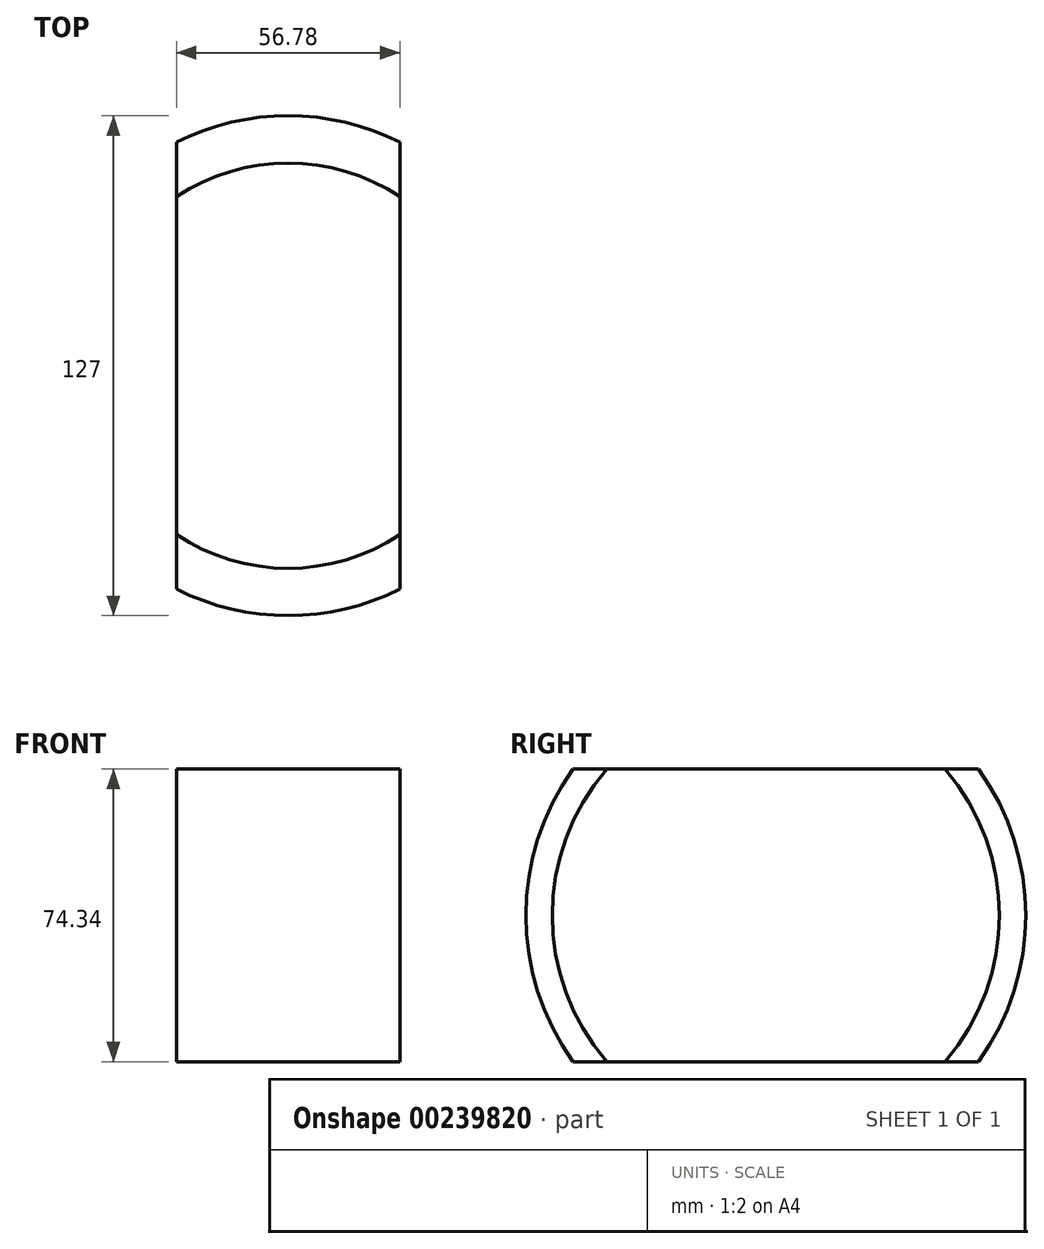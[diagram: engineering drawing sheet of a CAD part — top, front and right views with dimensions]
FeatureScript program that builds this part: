
annotation { "Feature Type Name" : "Feature", "Feature Type Description" : "" }
export const myFeature = defineFeature(function(context is Context, id is Id, definition is map)
    precondition{}
    {
        {
            var Q0;
            Q0=qCreatedBy(makeId("Front.planeOp"),FACE);
            var sketch = newSketch(context, id + "F0", { "sketchPlane" : qUnion([Q0])});
            skLineSegment(sketch, "E0.bottom", {"start": v(28.39, 37.17) * mm, "end": v(-28.39, 37.17) * mm});
            skLineSegment(sketch, "E0.top", {"start": v(28.39, -37.17) * mm, "end": v(-28.39, -37.17) * mm});
            skLineSegment(sketch, "E0.left", {"start": v(28.39, 37.17) * mm, "end": v(28.39, -37.17) * mm});
            skLineSegment(sketch, "E0.right", {"start": v(-28.39, 37.17) * mm, "end": v(-28.39, -37.17) * mm});
            skPoint(sketch, "E0.middle", {"position": v(0, 0) * mm});
            skSolve(sketch);
        }
        {
            var Q0;
            Q0 = qSketchRegion(id + "F0", true);
            extrude(context, id + "F1", {"entities" : qUnion([Q0]), "endBound" : BoundingType.SYMMETRIC, "depth" : 127 * mm});
        }
        {
            var Q0;
            Q0=qCreatedBy(makeId("Right.planeOp"),FACE);
            var sketch = newSketch(context, id + "F2", { "sketchPlane" : qUnion([Q0])});
            skArc(sketch, "E1", {"start": v(51.44, -37.23) * mm, "mid": v(63.5, 0) * mm, "end": v(51.44, 37.23) * mm});
            skLineSegment(sketch, "E2", {"start": v(51.44, 37.23) * mm, "end": v(51.44, -37.23) * mm, "construction": true});
            skLineSegment(sketch, "E3", {"start": v(0, 0) * mm, "end": v(51.44, 0) * mm, "construction": true});
            skLineSegment(sketch, "E4", {"start": v(51.44, 37.23) * mm, "end": v(80.73, 43.93) * mm});
            skLineSegment(sketch, "E5", {"start": v(80.73, 43.93) * mm, "end": v(80.73, -55.34) * mm});
            skLineSegment(sketch, "E6", {"start": v(80.73, -55.34) * mm, "end": v(51.44, -37.23) * mm});
            skLineSegment(sketch, "E7", {"start": v(0, 0) * mm, "end": v(0, -64.57) * mm, "construction": true});
            skSolve(sketch);
        }
        {
            var Q0;
            Q0 = qSketchRegion(id + "F2", true);
            var Q1;
            Q1=sQuery(id+"F2.wireOp",EDGE,"E7");
            revolve(context, id + "F3", {"operationType" : NewBodyOperationType.REMOVE, "entities" : qUnion([Q0]), "axis" : qUnion([Q1]), "revolveType" : RevolveType.FULL, "oppositeDirection" : true});
        }
    });
